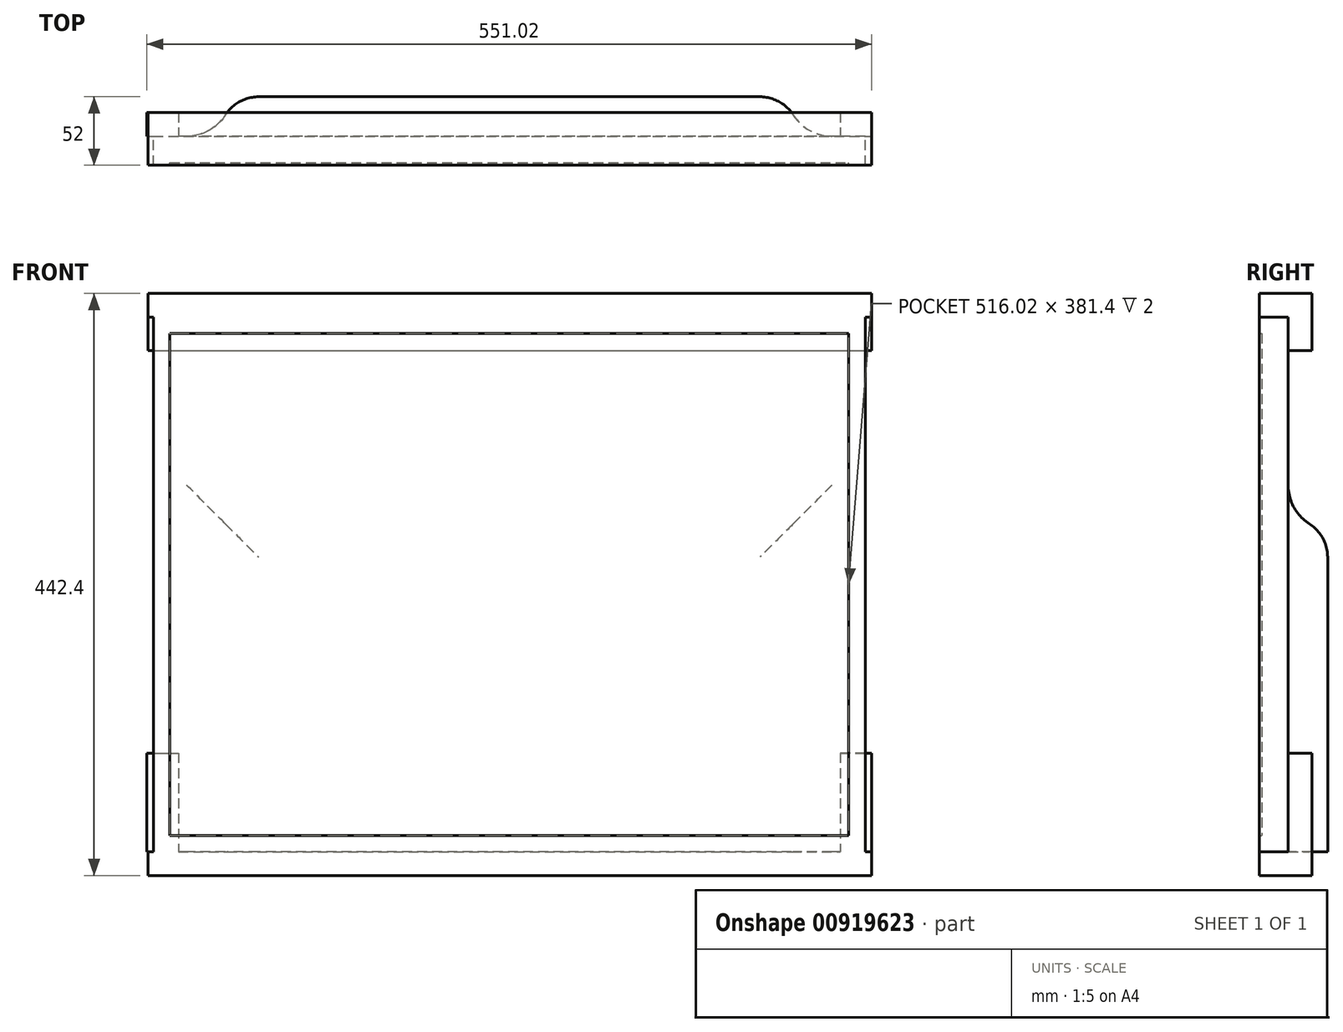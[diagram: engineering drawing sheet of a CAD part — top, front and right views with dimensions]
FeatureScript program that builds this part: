
annotation { "Feature Type Name" : "Feature", "Feature Type Description" : "" }
export const myFeature = defineFeature(function(context is Context, id is Id, definition is map)
    precondition{}
    {
        {
            var Q0;
            Q0=qCreatedBy(makeId("Front.planeOp"),FACE);
            var sketch = newSketch(context, id + "F0", { "sketchPlane" : qUnion([Q0])});
            skLineSegment(sketch, "E0.rect.bottom", {"start": v(270.51, -203.2) * mm, "end": v(-270.51, -203.2) * mm});
            skLineSegment(sketch, "E0.rect.top", {"start": v(270.5, 203.2) * mm, "end": v(-270.51, 203.2) * mm});
            skLineSegment(sketch, "E0.rect.left", {"start": v(270.51, -203.2) * mm, "end": v(270.5, 203.2) * mm});
            skLineSegment(sketch, "E0.rect.right", {"start": v(-270.51, -203.2) * mm, "end": v(-270.51, 203.2) * mm});
            skPoint(sketch, "E0.rect.middle", {"position": v(0, 0) * mm});
            skLineSegment(sketch, "E1.bottom", {"start": v(-258, 190.7) * mm, "end": v(258, 190.7) * mm});
            skLineSegment(sketch, "E1.top", {"start": v(-258.01, -190.7) * mm, "end": v(258.01, -190.7) * mm});
            skLineSegment(sketch, "E1.left", {"start": v(-258, 190.7) * mm, "end": v(-258.01, -190.7) * mm});
            skLineSegment(sketch, "E1.right", {"start": v(258, 190.7) * mm, "end": v(258.01, -190.7) * mm});
            skSolve(sketch);
        }
        {
            var Q0;
            Q0=qSketchRegion(id+"F0",true);
            extrude(context, id + "F1", {"entities" : qUnion([Q0]), "depth" : 22 * mm});
        }
        {
            var Q0;
            Q0=makeQuery(id+"F0.imprint","IMPRINT",FACE,{"disambiguationData":[TD([[makeQuery(id+"F0.imprint","IMPRINT",EDGE,{"derivedFrom":sQuery(id+"F0.wireOp",EDGE,"E1.bottom")}),-1.0]])]});
            extrude(context, id + "F2", {"entities" : qUnion([Q0]), "operationType" : NewBodyOperationType.ADD, "depth" : 20 * mm});
        }
        {
            var Q0;
            Q0=makeQuery(id+"F1.opExtrude","SWEPT_FACE",FACE,{"disambiguationData":[OSD([sQuery(id+"F0.wireOp",EDGE,"E0.rect.left")])]});
            var sketch = newSketch(context, id + "F3", { "sketchPlane" : qUnion([Q0])});
            skLineSegment(sketch, "E2", {"start": v(-22, -203.2) * mm, "end": v(-22, -221.2) * mm});
            skLineSegment(sketch, "E3", {"start": v(-22, -221.2) * mm, "end": v(18, -221.2) * mm});
            skLineSegment(sketch, "E4", {"start": v(18, -221.2) * mm, "end": v(18, -203.2) * mm});
            skLineSegment(sketch, "E5", {"start": v(0, -203.2) * mm, "end": v(-22, -203.2) * mm});
            skLineSegment(sketch, "E6.MirrorCS", {"start": v(18, 177.8) * mm, "end": v(0, 177.8) * mm});
            skLineSegment(sketch, "E7.MirrorCS", {"start": v(18, 221.2) * mm, "end": v(18, 177.8) * mm});
            skLineSegment(sketch, "E8.MirrorCS", {"start": v(0, 177.8) * mm, "end": v(0, 203.2) * mm});
            skLineSegment(sketch, "E9.MirrorCS", {"start": v(0, 203.2) * mm, "end": v(-22, 203.2) * mm});
            skLineSegment(sketch, "E10.MirrorCS", {"start": v(-22, 203.2) * mm, "end": v(-22, 221.2) * mm});
            skLineSegment(sketch, "E11.MirrorCS", {"start": v(-22, 221.2) * mm, "end": v(18, 221.2) * mm});
            skLineSegment(sketch, "E12", {"start": v(0, -203.2) * mm, "end": v(18, -203.2) * mm});
            skPoint(sketch, "E12.endSnap0", {"position": v(18, -199.5) * mm});
            skPoint(sketch, "E13.end.orphan", {"position": v(0, -177.8) * mm});
            skPoint(sketch, "E14.orphan", {"position": v(18, -177.8) * mm});
            skSolve(sketch);
        }
        {
            var Q0;
            Q0=makeQuery(id+"F3.imprint","IMPRINT",FACE,{"disambiguationData":[TD([[makeQuery(id+"F3.imprint","IMPRINT",EDGE,{"derivedFrom":sQuery(id+"F3.wireOp",EDGE,"E6.MirrorCS")}),-1.0]])]});
            var Q1;
            Q1=makeQuery(id+"F3.imprint","IMPRINT",FACE,{"disambiguationData":[TD([[makeQuery(id+"F3.imprint","IMPRINT",EDGE,{"derivedFrom":sQuery(id+"F3.wireOp",EDGE,"E2")}),1.0]])]});
            var Q2;
            Q2=makeQuery(id+"F1.opExtrude","SWEPT_FACE",FACE,{"disambiguationData":[OSD([sQuery(id+"F0.wireOp",EDGE,"E0.rect.right")])]});
            extrude(context, id + "F4", {"entities" : qUnion([Q0, Q1]), "oppositeDirection" : true, "endBoundEntityFace" : qUnion([Q2]), "offsetDistance" : 25 * mm, "depth" : 545 * mm, "hasSecondDirection" : true, "secondDirectionOppositeDirection" : false, "secondDirectionDepth" : 5 * mm});
        }
        {
            var Q0;
            {var subQ0=sQuery(id+"F0.wireOp",EDGE,"E1.bottom");var subQ1=sQuery(id+"F0.wireOp",EDGE,"E1.top");var subQ2=sQuery(id+"F0.wireOp",EDGE,"E1.left");var subQ3=sQuery(id+"F0.wireOp",EDGE,"E1.right");Q0=makeQuery(id+"F2.boolean.opBoolean","MERGE",FACE,{"derivedFrom":[makeQuery(id+"F1.opExtrude","CAP_FACE",FACE,{"disambiguationData":[OSD([sQuery(id+"F0.wireOp",EDGE,"E0.rect.bottom"),sQuery(id+"F0.wireOp",EDGE,"E0.rect.top"),sQuery(id+"F0.wireOp",EDGE,"E0.rect.left"),sQuery(id+"F0.wireOp",EDGE,"E0.rect.right"),subQ0,subQ1,subQ2,subQ3])],"isStart":true}),makeQuery(id+"F2.opExtrude","CAP_FACE",FACE,{"disambiguationData":[OSD([subQ0,subQ1,subQ2,subQ3])],"isStart":true})]});}
            var sketch = newSketch(context, id + "F5", { "sketchPlane" : qUnion([Q0])});
            skLineSegment(sketch, "E15.bottom", {"start": v(-220.5, 50.8) * mm, "end": v(220.51, 50.8) * mm});
            skLineSegment(sketch, "E15.top", {"start": v(-220.5, -203.2) * mm, "end": v(220.51, -203.2) * mm});
            skLineSegment(sketch, "E15.left", {"start": v(-220.51, 50.8) * mm, "end": v(-220.5, -203.2) * mm});
            skLineSegment(sketch, "E15.right", {"start": v(220.51, 50.8) * mm, "end": v(220.51, -203.2) * mm});
            skSolve(sketch);
        }
        {
            var Q0;
            Q0=makeQuery(id+"F5.imprint","IMPRINT",FACE,{"disambiguationData":[TD([[makeQuery(id+"F5.imprint","IMPRINT",EDGE,{"derivedFrom":sQuery(id+"F5.wireOp",EDGE,"E15.bottom")}),-1.0]])]});
            extrude(context, id + "F6", {"entities" : qUnion([Q0]), "operationType" : NewBodyOperationType.ADD, "depth" : 30 * mm});
        }
        {
            var Q0;
            Q0=makeQuery(id+"F6.opExtrude","CAP_EDGE",EDGE,{"disambiguationData":[OSD([sQuery(id+"F5.wireOp",EDGE,"E15.right")])],"isStart":false});
            var Q1;
            Q1=makeQuery(id+"F6.opExtrude","CAP_EDGE",EDGE,{"disambiguationData":[OSD([sQuery(id+"F5.wireOp",EDGE,"E15.bottom")])],"isStart":false});
            var Q2;
            Q2=makeQuery(id+"F6.opExtrude","CAP_EDGE",EDGE,{"disambiguationData":[OSD([sQuery(id+"F5.wireOp",EDGE,"E15.left")])],"isStart":false});
            fillet(context, id + "F7", {"entities" : qUnion([Q0, Q1, Q2]), "radius" : 30 * mm, "tangentPropagation" : true, "allowEdgeOverflow" : false});
        }
        {
            var Q0;
            Q0=makeQuery(id+"F12.opBoolean","MERGE",FACE,{"derivedFrom":[makeQuery(id+"F1.opExtrude","CAP_FACE",FACE,{"disambiguationData":[OSD([sQuery(id+"F0.wireOp",EDGE,"E0.rect.bottom"),sQuery(id+"F0.wireOp",EDGE,"E0.rect.top"),sQuery(id+"F0.wireOp",EDGE,"E0.rect.left"),sQuery(id+"F0.wireOp",EDGE,"E0.rect.right"),sQuery(id+"F0.wireOp",EDGE,"E1.bottom"),sQuery(id+"F0.wireOp",EDGE,"E1.top"),sQuery(id+"F0.wireOp",EDGE,"E1.left"),sQuery(id+"F0.wireOp",EDGE,"E1.right")])],"isStart":false}),makeQuery(id+"F4.opExtrude","SWEPT_FACE",FACE,{"disambiguationData":[OSD([sQuery(id+"F3.wireOp",EDGE,"E2")])]}),makeQuery(id+"F4.opExtrude","SWEPT_FACE",FACE,{"disambiguationData":[OSD([sQuery(id+"F3.wireOp",EDGE,"E10.MirrorCS")])]})]});
            var sketch = newSketch(context, id + "F8", { "sketchPlane" : qUnion([Q0])});
            skLineSegment(sketch, "E16.bottom", {"start": v(-274.5, 221.2) * mm, "end": v(275.51, 221.2) * mm});
            skLineSegment(sketch, "E16.top", {"start": v(-274.5, -221.2) * mm, "end": v(275.51, -221.2) * mm});
            skLineSegment(sketch, "E16.left", {"start": v(-274.5, 221.2) * mm, "end": v(-274.5, -221.2) * mm});
            skLineSegment(sketch, "E16.right", {"start": v(275.51, 221.2) * mm, "end": v(275.51, -221.2) * mm});
            skSolve(sketch);
        }
        {
            var Q0;
            {var subQ0=sQuery(id+"F0.wireOp",EDGE,"E1.right");var subQ1=sQuery(id+"F0.wireOp",EDGE,"E1.left");var subQ2=sQuery(id+"F0.wireOp",EDGE,"E1.top");var subQ3=sQuery(id+"F0.wireOp",EDGE,"E1.bottom");Q0=makeQuery(id+"F7.opFillet","BLEND_EDGE",EDGE,{"blendedFrom":[makeQuery(id+"F6.opExtrude","CAP_EDGE",EDGE,{"disambiguationData":[OSD([sQuery(id+"F5.wireOp",EDGE,"E15.bottom")])],"isStart":false}),makeQuery(id+"F2.boolean.opBoolean","MERGE",FACE,{"derivedFrom":[makeQuery(id+"F1.opExtrude","CAP_FACE",FACE,{"disambiguationData":[OSD([sQuery(id+"F0.wireOp",EDGE,"E0.rect.bottom"),sQuery(id+"F0.wireOp",EDGE,"E0.rect.top"),sQuery(id+"F0.wireOp",EDGE,"E0.rect.left"),sQuery(id+"F0.wireOp",EDGE,"E0.rect.right"),subQ3,subQ2,subQ1,subQ0])],"isStart":true}),makeQuery(id+"F2.opExtrude","CAP_FACE",FACE,{"disambiguationData":[OSD([subQ3,subQ2,subQ1,subQ0])],"isStart":true})]})],"blendedInto":[makeQuery(id+"F2.boolean.opBoolean","MERGE",FACE,{"derivedFrom":[makeQuery(id+"F1.opExtrude","CAP_FACE",FACE,{"disambiguationData":[OSD([sQuery(id+"F0.wireOp",EDGE,"E0.rect.bottom"),sQuery(id+"F0.wireOp",EDGE,"E0.rect.top"),sQuery(id+"F0.wireOp",EDGE,"E0.rect.left"),sQuery(id+"F0.wireOp",EDGE,"E0.rect.right"),subQ3,subQ2,subQ1,subQ0])],"isStart":true}),makeQuery(id+"F2.opExtrude","CAP_FACE",FACE,{"disambiguationData":[OSD([subQ3,subQ2,subQ1,subQ0])],"isStart":true})]})]});}
            var Q1;
            {var subQ0=sQuery(id+"F0.wireOp",EDGE,"E1.right");var subQ1=sQuery(id+"F0.wireOp",EDGE,"E1.left");var subQ2=sQuery(id+"F0.wireOp",EDGE,"E1.top");var subQ3=sQuery(id+"F0.wireOp",EDGE,"E1.bottom");Q1=makeQuery(id+"F7.opFillet","BLEND_EDGE",EDGE,{"blendedFrom":[makeQuery(id+"F6.opExtrude","CAP_EDGE",EDGE,{"disambiguationData":[OSD([sQuery(id+"F5.wireOp",EDGE,"E15.left")])],"isStart":false}),makeQuery(id+"F2.boolean.opBoolean","MERGE",FACE,{"derivedFrom":[makeQuery(id+"F1.opExtrude","CAP_FACE",FACE,{"disambiguationData":[OSD([sQuery(id+"F0.wireOp",EDGE,"E0.rect.bottom"),sQuery(id+"F0.wireOp",EDGE,"E0.rect.top"),sQuery(id+"F0.wireOp",EDGE,"E0.rect.left"),sQuery(id+"F0.wireOp",EDGE,"E0.rect.right"),subQ3,subQ2,subQ1,subQ0])],"isStart":true}),makeQuery(id+"F2.opExtrude","CAP_FACE",FACE,{"disambiguationData":[OSD([subQ3,subQ2,subQ1,subQ0])],"isStart":true})]})],"blendedInto":[makeQuery(id+"F2.boolean.opBoolean","MERGE",FACE,{"derivedFrom":[makeQuery(id+"F1.opExtrude","CAP_FACE",FACE,{"disambiguationData":[OSD([sQuery(id+"F0.wireOp",EDGE,"E0.rect.bottom"),sQuery(id+"F0.wireOp",EDGE,"E0.rect.top"),sQuery(id+"F0.wireOp",EDGE,"E0.rect.left"),sQuery(id+"F0.wireOp",EDGE,"E0.rect.right"),subQ3,subQ2,subQ1,subQ0])],"isStart":true}),makeQuery(id+"F2.opExtrude","CAP_FACE",FACE,{"disambiguationData":[OSD([subQ3,subQ2,subQ1,subQ0])],"isStart":true})]})]});}
            var Q2;
            {var subQ0=sQuery(id+"F0.wireOp",EDGE,"E1.right");var subQ1=sQuery(id+"F0.wireOp",EDGE,"E1.left");var subQ2=sQuery(id+"F0.wireOp",EDGE,"E1.top");var subQ3=sQuery(id+"F0.wireOp",EDGE,"E1.bottom");Q2=makeQuery(id+"F7.opFillet","BLEND_EDGE",EDGE,{"blendedFrom":[makeQuery(id+"F6.opExtrude","CAP_EDGE",EDGE,{"disambiguationData":[OSD([sQuery(id+"F5.wireOp",EDGE,"E15.right")])],"isStart":false}),makeQuery(id+"F2.boolean.opBoolean","MERGE",FACE,{"derivedFrom":[makeQuery(id+"F1.opExtrude","CAP_FACE",FACE,{"disambiguationData":[OSD([sQuery(id+"F0.wireOp",EDGE,"E0.rect.bottom"),sQuery(id+"F0.wireOp",EDGE,"E0.rect.top"),sQuery(id+"F0.wireOp",EDGE,"E0.rect.left"),sQuery(id+"F0.wireOp",EDGE,"E0.rect.right"),subQ3,subQ2,subQ1,subQ0])],"isStart":true}),makeQuery(id+"F2.opExtrude","CAP_FACE",FACE,{"disambiguationData":[OSD([subQ3,subQ2,subQ1,subQ0])],"isStart":true})]})],"blendedInto":[makeQuery(id+"F2.boolean.opBoolean","MERGE",FACE,{"derivedFrom":[makeQuery(id+"F1.opExtrude","CAP_FACE",FACE,{"disambiguationData":[OSD([sQuery(id+"F0.wireOp",EDGE,"E0.rect.bottom"),sQuery(id+"F0.wireOp",EDGE,"E0.rect.top"),sQuery(id+"F0.wireOp",EDGE,"E0.rect.left"),sQuery(id+"F0.wireOp",EDGE,"E0.rect.right"),subQ3,subQ2,subQ1,subQ0])],"isStart":true}),makeQuery(id+"F2.opExtrude","CAP_FACE",FACE,{"disambiguationData":[OSD([subQ3,subQ2,subQ1,subQ0])],"isStart":true})]})]});}
            fillet(context, id + "F9", {"entities" : qUnion([Q0, Q1, Q2]), "radius" : 35 * mm, "tangentPropagation" : true, "allowEdgeOverflow" : false});
        }
        {
            var Q0;
            Q0=makeQuery(id+"F4.opExtrude","SWEPT_FACE",FACE,{"disambiguationData":[OSD([sQuery(id+"F3.wireOp",EDGE,"E5"),sQuery(id+"F3.wireOp",EDGE,"E12")])]});
            var sketch = newSketch(context, id + "F10", { "sketchPlane" : qUnion([Q0])});
            skLineSegment(sketch, "E17.bottom", {"start": v(275.5, 18) * mm, "end": v(251.49, 18) * mm});
            skLineSegment(sketch, "E17.top", {"start": v(275.5, 0) * mm, "end": v(251.49, 0) * mm});
            skLineSegment(sketch, "E17.left", {"start": v(275.5, 18) * mm, "end": v(275.5, 0) * mm});
            skLineSegment(sketch, "E17.right", {"start": v(251.49, 18) * mm, "end": v(251.49, 0) * mm});
            skLineSegment(sketch, "E18.MirrorCS", {"start": v(-251.49, 18) * mm, "end": v(-251.49, 0) * mm});
            skLineSegment(sketch, "E19.MirrorCS", {"start": v(-275.51, 18) * mm, "end": v(-251.49, 18) * mm});
            skLineSegment(sketch, "E20.MirrorCS", {"start": v(-275.51, 18) * mm, "end": v(-275.51, 0) * mm});
            skLineSegment(sketch, "E21.MirrorCS", {"start": v(-275.51, 0) * mm, "end": v(-251.49, 0) * mm});
            skSolve(sketch);
        }
        {
            var Q0;
            {var subQ0=sQuery(id+"F10.wireOp",EDGE,"E18.MirrorCS");Q0=makeQuery(id+"F10.imprint","IMPRINT",FACE,{"disambiguationData":[TD([[makeQuery(id+"F10.imprint","IMPRINT",EDGE,{"derivedFrom":subQ0}),-1.0]])]});}
            var Q1;
            Q1=makeQuery(id+"F10.imprint","IMPRINT",FACE,{"disambiguationData":[TD([[makeQuery(id+"F10.imprint","IMPRINT",EDGE,{"derivedFrom":sQuery(id+"F10.wireOp",EDGE,"E17.bottom")}),-1.0]])]});
            extrude(context, id + "F11", {"entities" : qUnion([Q0, Q1]), "depth" : 75 * mm, "offsetDistance" : 25 * mm});
        }
        {
            var Q0;
            Q0=makeQuery(id+"F4.opExtrude","SWEPT_BODY",BODY,{"disambiguationData":[OSD([sQuery(id+"F3.wireOp",EDGE,"E2"),sQuery(id+"F3.wireOp",EDGE,"E3"),sQuery(id+"F3.wireOp",EDGE,"E4"),sQuery(id+"F3.wireOp",EDGE,"E13"),sQuery(id+"F3.wireOp",EDGE,"6dceea47-eba1-4fc9-aad4-764a96a452da"),sQuery(id+"F3.wireOp",EDGE,"E5")])]});
            var Q1;
            Q1=makeQuery(id+"F4.opExtrude","SWEPT_BODY",BODY,{"disambiguationData":[OSD([sQuery(id+"F3.wireOp",EDGE,"E6.MirrorCS"),sQuery(id+"F3.wireOp",EDGE,"E7.MirrorCS"),sQuery(id+"F3.wireOp",EDGE,"E8.MirrorCS"),sQuery(id+"F3.wireOp",EDGE,"E9.MirrorCS"),sQuery(id+"F3.wireOp",EDGE,"E10.MirrorCS"),sQuery(id+"F3.wireOp",EDGE,"E11.MirrorCS")])]});
            var Q2;
            Q2=makeQuery(id+"F1.opExtrude","SWEPT_BODY",BODY,{"disambiguationData":[OSD([sQuery(id+"F0.wireOp",EDGE,"E0.rect.bottom"),sQuery(id+"F0.wireOp",EDGE,"E0.rect.top"),sQuery(id+"F0.wireOp",EDGE,"E0.rect.left"),sQuery(id+"F0.wireOp",EDGE,"E0.rect.right"),sQuery(id+"F0.wireOp",EDGE,"E1.bottom"),sQuery(id+"F0.wireOp",EDGE,"E1.top"),sQuery(id+"F0.wireOp",EDGE,"E1.left"),sQuery(id+"F0.wireOp",EDGE,"E1.right")])]});
            var Q3;
            Q3=makeQuery(id+"F11.opExtrude","SWEPT_BODY",BODY,{"disambiguationData":[OSD([sQuery(id+"F10.wireOp",EDGE,"E17.bottom"),sQuery(id+"F10.wireOp",EDGE,"E17.top"),sQuery(id+"F10.wireOp",EDGE,"E17.left"),sQuery(id+"F10.wireOp",EDGE,"E17.right")])]});
            var Q4;
            Q4=makeQuery(id+"F11.opExtrude","SWEPT_BODY",BODY,{"disambiguationData":[OSD([sQuery(id+"F3.wireOp",EDGE,"E5"),sQuery(id+"F3.wireOp",EDGE,"E12"),sQuery(id+"F10.wireOp",EDGE,"E18.MirrorCS"),sQuery(id+"F10.wireOp",EDGE,"E19.MirrorCS"),sQuery(id+"F10.wireOp",EDGE,"E21.MirrorCS")])]});
            booleanBodies(context, id + "F12", {"operationType" : BooleanOperationType.UNION, "tools" : qUnion([Q0, Q1, Q2, Q3, Q4])});
        }
    });
